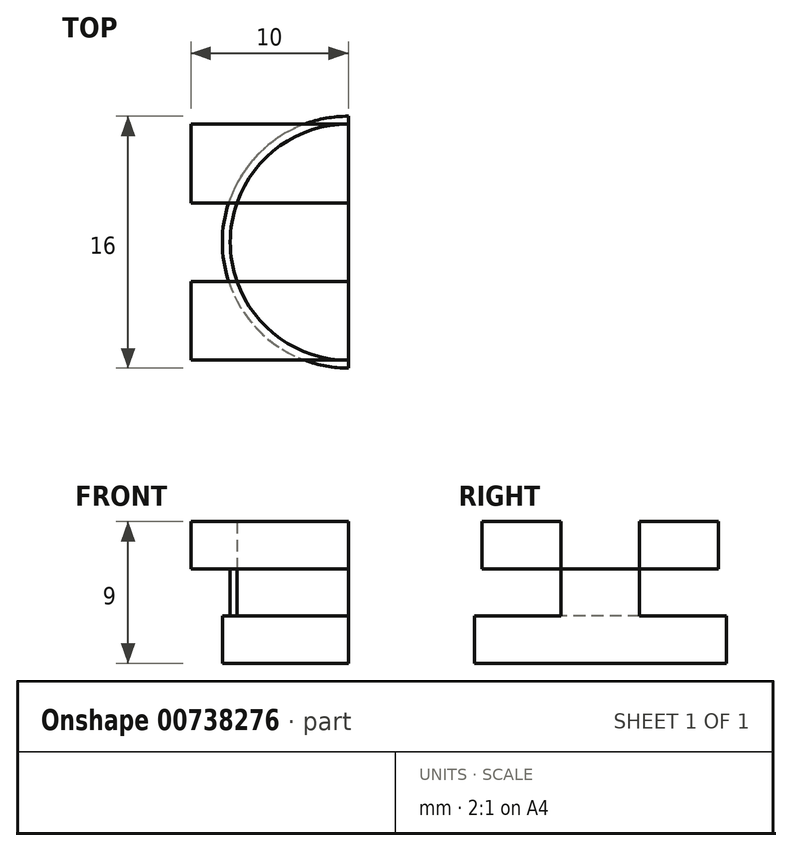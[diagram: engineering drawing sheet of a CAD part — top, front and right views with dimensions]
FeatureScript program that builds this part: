
annotation { "Feature Type Name" : "Feature", "Feature Type Description" : "" }
export const myFeature = defineFeature(function(context is Context, id is Id, definition is map)
    precondition{}
    {
        {
            var Q0;
            Q0=qCreatedBy(makeId("Top.planeOp"),FACE);
            var sketch = newSketch(context, id + "F0", { "sketchPlane" : qUnion([Q0])});
            skCircle(sketch, "E0", {"center": v(0, 0) * mm, "radius": 7.5 * mm});
            skLineSegment(sketch, "E1", {"start": v(0, 0) * mm, "end": v(0, -7.5) * mm});
            skLineSegment(sketch, "E2", {"start": v(0, -7.5) * mm, "end": v(0, 7.5) * mm});
            skLineSegment(sketch, "E3.bottom", {"start": v(0, -7.5) * mm, "end": v(-10, -7.5) * mm});
            skLineSegment(sketch, "E3.top", {"start": v(0, -2.5) * mm, "end": v(-10, -2.5) * mm});
            skLineSegment(sketch, "E3.left", {"start": v(0, -7.5) * mm, "end": v(0, -2.5) * mm});
            skLineSegment(sketch, "E3.right", {"start": v(-10, -7.5) * mm, "end": v(-10, -2.5) * mm});
            skLineSegment(sketch, "E4.bottom", {"start": v(0, 7.5) * mm, "end": v(-10, 7.5) * mm});
            skLineSegment(sketch, "E4.top", {"start": v(0, 2.5) * mm, "end": v(-10, 2.5) * mm});
            skLineSegment(sketch, "E4.left", {"start": v(0, 7.5) * mm, "end": v(0, 2.5) * mm});
            skLineSegment(sketch, "E4.right", {"start": v(-10, 7.5) * mm, "end": v(-10, 2.5) * mm});
            skSolve(sketch);
        }
        {
            var Q0;
            {var subQ3=sQuery(id+"F0.wireOp",EDGE,"E0");var subQ5=sQuery(id+"F0.wireOp",EDGE,"E4.top");var subQ8=makeQuery(id+"F0.imprint","INTERSECT",VERTEX,{"derivedFrom":[subQ3,subQ5]});Q0=makeQuery(id+"F0.imprint","IMPRINT",FACE,{"disambiguationData":[TD([[makeQuery(id+"F0.imprint","IMPRINT",EDGE,{"disambiguationData":[TD([[subQ8,-1.0]])],"derivedFrom":subQ3}),1.0]])]});}
            var Q1;
            {var subQ0=sQuery(id+"F0.wireOp",EDGE,"E3.left");Q1=makeQuery(id+"F0.imprint","IMPRINT",FACE,{"disambiguationData":[TD([[makeQuery(id+"F0.imprint","IMPRINT",EDGE,{"derivedFrom":subQ0}),1.0]])]});}
            var Q2;
            {var subQ0=sQuery(id+"F0.wireOp",EDGE,"E4.left");Q2=makeQuery(id+"F0.imprint","IMPRINT",FACE,{"disambiguationData":[TD([[makeQuery(id+"F0.imprint","IMPRINT",EDGE,{"derivedFrom":subQ0}),-1.0]])]});}
            extrude(context, id + "F1", {"entities" : qUnion([Q0, Q1, Q2]), "depth" : -3 * mm, "offsetDistance" : 25 * mm});
        }
        {
            var Q0;
            {var subQ0=sQuery(id+"F0.wireOp",EDGE,"E4.bottom");Q0=makeQuery(id+"F0.imprint","IMPRINT",FACE,{"disambiguationData":[TD([[makeQuery(id+"F0.imprint","IMPRINT",EDGE,{"derivedFrom":subQ0}),1.0]])]});}
            var Q1;
            {var subQ0=sQuery(id+"F0.wireOp",EDGE,"E4.left");Q1=makeQuery(id+"F0.imprint","IMPRINT",FACE,{"disambiguationData":[TD([[makeQuery(id+"F0.imprint","IMPRINT",EDGE,{"derivedFrom":subQ0}),-1.0]])]});}
            var Q2;
            {var subQ0=sQuery(id+"F0.wireOp",EDGE,"E3.bottom");Q2=makeQuery(id+"F0.imprint","IMPRINT",FACE,{"disambiguationData":[TD([[makeQuery(id+"F0.imprint","IMPRINT",EDGE,{"derivedFrom":subQ0}),-1.0]])]});}
            var Q3;
            {var subQ0=sQuery(id+"F0.wireOp",EDGE,"E3.left");Q3=makeQuery(id+"F0.imprint","IMPRINT",FACE,{"disambiguationData":[TD([[makeQuery(id+"F0.imprint","IMPRINT",EDGE,{"derivedFrom":subQ0}),1.0]])]});}
            extrude(context, id + "F2", {"entities" : qUnion([Q0, Q1, Q2, Q3]), "operationType" : NewBodyOperationType.ADD, "depth" : 3 * mm, "offsetDistance" : 25 * mm});
        }
        {
            var Q0;
            Q0=makeQuery(id+"F1.opExtrude","CAP_FACE",FACE,{"disambiguationData":[OSD([sQuery(id+"F0.wireOp",EDGE,"E0"),sQuery(id+"F0.wireOp",EDGE,"E2"),sQuery(id+"F0.wireOp",EDGE,"E3.left"),sQuery(id+"F0.wireOp",EDGE,"E4.left")])],"isStart":false});
            var sketch = newSketch(context, id + "F3", { "sketchPlane" : qUnion([Q0])});
            skCircle(sketch, "E5", {"center": v(0, 0) * mm, "radius": 8 * mm});
            skLineSegment(sketch, "E6", {"start": v(0, 7.5) * mm, "end": v(0, 8) * mm});
            skLineSegment(sketch, "E7", {"start": v(0, 8) * mm, "end": v(0, -8) * mm});
            skSolve(sketch);
        }
        {
            var Q0;
            {var subQ4=makeQuery(id+"F1.opExtrude","CAP_EDGE",EDGE,{"disambiguationData":[OSD([sQuery(id+"F0.wireOp",EDGE,"E0")])],"isStart":false});Q0=makeQuery(id+"F3.imprint","IMPRINT",FACE,{"disambiguationData":[TD([[makeQuery(id+"F3.imprint","IMPRINT",EDGE,{"derivedFrom":subQ4}),1.0]])]});}
            var Q1;
            {var subQ1=makeQuery(id+"F1.opExtrude","CAP_EDGE",EDGE,{"disambiguationData":[OSD([sQuery(id+"F0.wireOp",EDGE,"E0")])],"isStart":false});Q1=makeQuery(id+"F3.imprint","IMPRINT",FACE,{"disambiguationData":[TD([[makeQuery(id+"F3.imprint","IMPRINT",EDGE,{"derivedFrom":subQ1}),-1.0]])]});}
            extrude(context, id + "F4", {"entities" : qUnion([Q0, Q1]), "operationType" : NewBodyOperationType.ADD, "depth" : 3 * mm, "offsetDistance" : 25 * mm});
        }
    });
